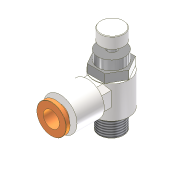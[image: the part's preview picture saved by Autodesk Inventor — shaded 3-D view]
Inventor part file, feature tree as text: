
AUTODESK INVENTOR PART (.ipt)
format: ipt  version: unknown  size: 277,504 bytes
history: native  units: mm
features: extrude x12, sketch x12, plane x2, fillet x2, chamfer x1, thread x1, projected_geometry x1
ambient origin geometry x8: Origin, YZ Plane, XZ Plane, XY Plane, X Axis, Y Axis, Z Axis, Center Point
feature tree (31):
  extrude  "Extrusion1"  Depth=13.0mm TaperAngle=0.0deg
  extrude  "Extrusion2"  Depth=10.9mm
  extrude  "Extrusion3"  Depth=3.9mm
  extrude  "Extrusion4"  Depth=4.5mm TaperAngle=0.0deg
  extrude  "Extrusion5"  Depth=7.5mm
  extrude  "Extrusion6"  Depth=7.5mm TaperAngle=0.0deg
  extrude  "Extrusion7"  Depth=10.0mm
  plane  "Work Plane1"
  extrude  "Extrusion8"  Depth=7.5mm TaperAngle=0.0deg
  extrude  "Extrusion9"  Depth=11.0mm TaperAngle=0.0deg
  chamfer  "Chamfer1"  Distance=2.0mm Angle=45.0deg
  extrude  "Extrusion10"  Depth=11.0mm TaperAngle=0.0deg
  plane  "Work Plane2"
  extrude  "Extrusion11"  Depth=6.5mm
  extrude  "Extrusion12"  Depth=11.9mm
  fillet  "Fillet1"  Radius=1.6mm
  fillet  "Fillet2"  Radius=0.1mm
  thread  "Thread1"  [1 undecoded]
  sketch  "Sketch1"  dims[d0=14.2mm d1=13.0mm d2=0.0mm]
  sketch  "Sketch2"  dims[d3=3.4mm d4=0.0mm d5=10.9mm]
  sketch  "Sketch3"  dims[d6=3.8mm d7=0.0mm d8=3.9mm]
  sketch  "Sketch4"  dims[d9=3.0mm d10=0.0mm d11=4.5mm d12=0.0mm]
  sketch  "Sketch5"  dims[d13=10.1mm d14=7.5mm d15=-0.174533mm]
  sketch  "Sketch6"  dims[d16=5.9mm d17=7.5mm d18=0.0mm]
  sketch  "Sketch7"  dims[d19=-9.6mm d20=10.0mm]
  sketch  "Sketch8"  dims[d21=0.2mm d22=7.5mm d23=0.0mm]
  projected_geometry  "Projected Loop1"
  sketch  "Sketch9"  dims[d24=13.5mm d25=11.0mm d26=0.0mm d27=2.0mm d28=2.0mm d29=45.0deg]
  sketch  "Sketch10"  dims[d30=7.25mm d31=11.0mm d32=0.0mm]
  sketch  "Sketch11"  dims[d33=2.0mm d34=6.5mm]
  sketch  "Sketch12"  dims[d35=11.0mm d36=0.0mm d37=11.9mm d38=1.6mm d39=0.0mm d40=0.1mm d41=0.2mm d42=10.0mm d43=0.0mm]
note: 1 required parameter value undecoded (feature->parameter linkage not recoverable at this tier; creation-order binding heuristic only, values carry confidence <= 0.55)
